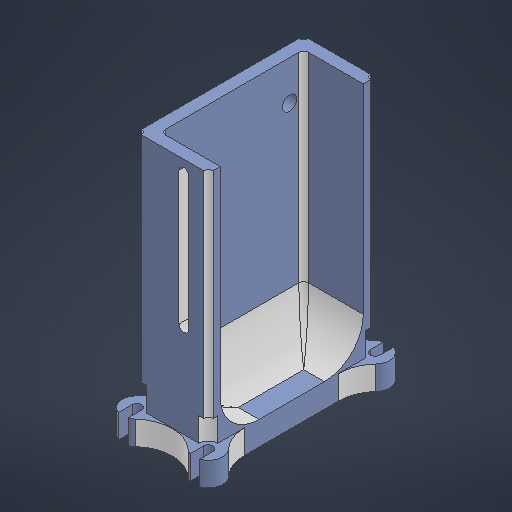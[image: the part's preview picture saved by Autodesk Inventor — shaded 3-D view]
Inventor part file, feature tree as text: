
AUTODESK INVENTOR PART (.ipt)
format: ipt  version: 2025.1 (Build 291241000, 241)  size: 740,864 bytes
history: native  units: in
note: dims shown in document units (in); Inventor stores cm internally (conversion verified against a paired STEP export)
features: extrude x7, sketch x7, fillet x3, plane x1, other x1
ambient origin geometry x8: Origin, YZ Plane, XZ Plane, XY Plane, X Axis, Y Axis, Z Axis, Center Point
bodies: Solid1 (feature_tree)
feature tree (19):
  extrude  "Extrusion1"  Depth=2.7559in
  extrude  "Extrusion2"  Depth=0.4724in
  extrude  "Extrusion3"  Depth=0.4724in
  extrude  "Extrusion4"  Depth=0.3937in TaperAngle=0.0deg
  plane  "Work Plane1"
  extrude  "Extrusion5"  Depth=0.1575in
  extrude  "Extrusion6"  Depth=0.1575in
  fillet  "Fillet1"  Radius=0.1575in
  extrude  "Extrusion7"  Depth=0.1575in
  fillet  "Fillet2"  Radius=0.1575in
  fillet  "Fillet3"  Radius=4.6599in
  sketch  "Sketch1"  dims[d0=1.1811in d1=2.7559in]
  sketch  "Sketch2"  dims[d2=4.3307in d3=0.0in d4=0.4724in]
  sketch  "Sketch3"  dims[d5=0.4724in d6=0.4724in]
  sketch  "Sketch4"  dims[d7=0.4724in d8=0.3937in d9=0.0in]
  sketch  "Sketch6"  dims[d10=0.1575in d11=0.1575in]
  sketch  "Sketch7"  dims[d12=0.1575in d13=0.1575in d14=0.1575in]
  sketch  "Sketch8"  dims[d15=0.1575in d16=0.1575in d17=0.1575in d18=4.6599in d19=0.0in d20=0.6496in d21=0.8268in d22=0.122in d23=0.2362in d24=4.6599in d25=0.0in d26=-0.6496in d42=1.1811in d43=2.7559in d44=0.7874in d45=2.3622in d46=3.8937in d47=0.0in d48=0.3248in d49=0.1969in d50=1.1811in d51=0.1614in d52=0.1614in d53=0.3937in d54=0.0in d55=0.7874in d56=0.1614in d57=0.6412in d58=0.315in d59=0.315in d60=0.315in d61=0.315in d62=0.3937in d63=0.0in d64=0.6412in d65=0.0787in]
  other  "Finish1"
